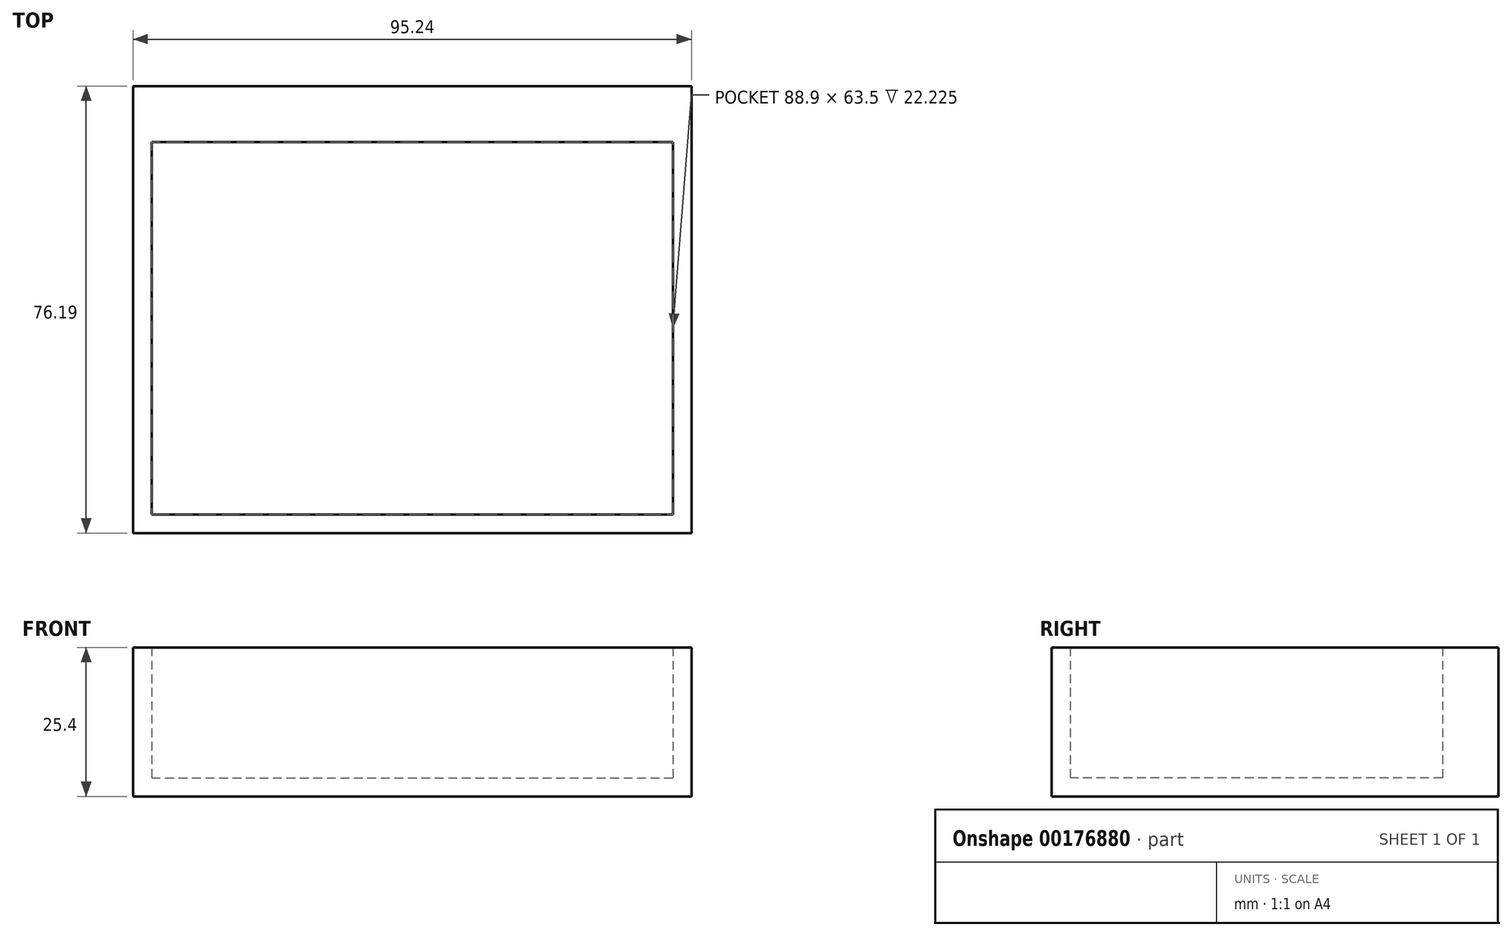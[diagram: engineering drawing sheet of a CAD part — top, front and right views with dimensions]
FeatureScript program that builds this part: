
annotation { "Feature Type Name" : "Feature", "Feature Type Description" : "" }
export const myFeature = defineFeature(function(context is Context, id is Id, definition is map)
    precondition{}
    {
        {
            var Q0;
            Q0=qCreatedBy(makeId("Top.planeOp"),FACE);
            var sketch = newSketch(context, id + "F0", { "sketchPlane" : qUnion([Q0])});
            skLineSegment(sketch, "E0.bottom", {"start": v(44.45, 31.75) * mm, "end": v(-44.45, 31.75) * mm});
            skLineSegment(sketch, "E0.top", {"start": v(44.45, -31.75) * mm, "end": v(-44.45, -31.75) * mm});
            skLineSegment(sketch, "E0.left", {"start": v(44.45, 31.75) * mm, "end": v(44.45, -31.75) * mm});
            skLineSegment(sketch, "E0.right", {"start": v(-44.45, 31.75) * mm, "end": v(-44.45, -31.75) * mm});
            skPoint(sketch, "E0.middle", {"position": v(0, 0) * mm});
            skLineSegment(sketch, "E1.bottom", {"start": v(-47.62, -34.92) * mm, "end": v(47.63, -34.92) * mm});
            skLineSegment(sketch, "E1.top", {"start": v(-47.63, 41.28) * mm, "end": v(47.62, 41.28) * mm});
            skLineSegment(sketch, "E1.left", {"start": v(-47.62, -34.92) * mm, "end": v(-47.62, 41.28) * mm});
            skLineSegment(sketch, "E1.right", {"start": v(47.63, -34.92) * mm, "end": v(47.62, 41.28) * mm});
            skLineSegment(sketch, "E2", {"start": v(-44.45, -31.75) * mm, "end": v(-47.62, -31.75) * mm, "construction": true});
            skLineSegment(sketch, "E3", {"start": v(44.45, -31.75) * mm, "end": v(47.63, -31.75) * mm, "construction": true});
            skLineSegment(sketch, "E4", {"start": v(-44.45, -31.75) * mm, "end": v(-44.45, -34.92) * mm, "construction": true});
            skSolve(sketch);
        }
        {
            var Q0;
            Q0=makeQuery(id+"F0.imprint","IMPRINT",FACE,{"disambiguationData":[TD([[makeQuery(id+"F0.imprint","IMPRINT",EDGE,{"derivedFrom":sQuery(id+"F0.wireOp",EDGE,"E0.bottom")}),-1.0]])]});
            extrude(context, id + "F1", {"entities" : qUnion([Q0]), "depth" : 25.4 * mm});
        }
        {
            var Q0;
            Q0=qCreatedBy(makeId("Top.planeOp"),FACE);
            var sketch = newSketch(context, id + "F2", { "sketchPlane" : qUnion([Q0])});
            skLineSegment(sketch, "E5.bottom", {"start": v(-44.45, 31.75) * mm, "end": v(44.45, 31.75) * mm});
            skLineSegment(sketch, "E5.top", {"start": v(-44.45, -31.75) * mm, "end": v(44.45, -31.75) * mm});
            skLineSegment(sketch, "E5.left", {"start": v(-44.45, 31.75) * mm, "end": v(-44.45, -31.75) * mm});
            skLineSegment(sketch, "E5.right", {"start": v(44.45, 31.75) * mm, "end": v(44.45, -31.75) * mm});
            skSolve(sketch);
        }
        {
            var Q0;
            Q0 = qSketchRegion(id + "F2", true);
            extrude(context, id + "F3", {"entities" : qUnion([Q0]), "operationType" : NewBodyOperationType.ADD, "depth" : 3.17 * mm});
        }
    });
